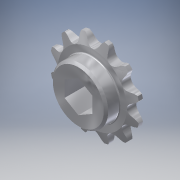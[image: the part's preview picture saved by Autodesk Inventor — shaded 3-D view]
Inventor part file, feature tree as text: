
AUTODESK INVENTOR PART (.ipt)
format: ipt  version: 2016 (Build 200138000, 138)  size: 483,328 bytes
history: native  units: in
note: dims shown in document units (in); Inventor stores cm internally (conversion verified against a paired STEP export)
features: chamfer x1
ambient origin geometry x8: Origin, YZ Plane, XZ Plane, XY Plane, X Axis, Y Axis, Z Axis, Center Point
bodies: Solid1 (feature_tree)
feature tree (1):
  chamfer  "Chamfer1"  [1 undecoded]
note: 1 required parameter value undecoded (feature->parameter linkage not recoverable at this tier; creation-order binding heuristic only, values carry confidence <= 0.55)
